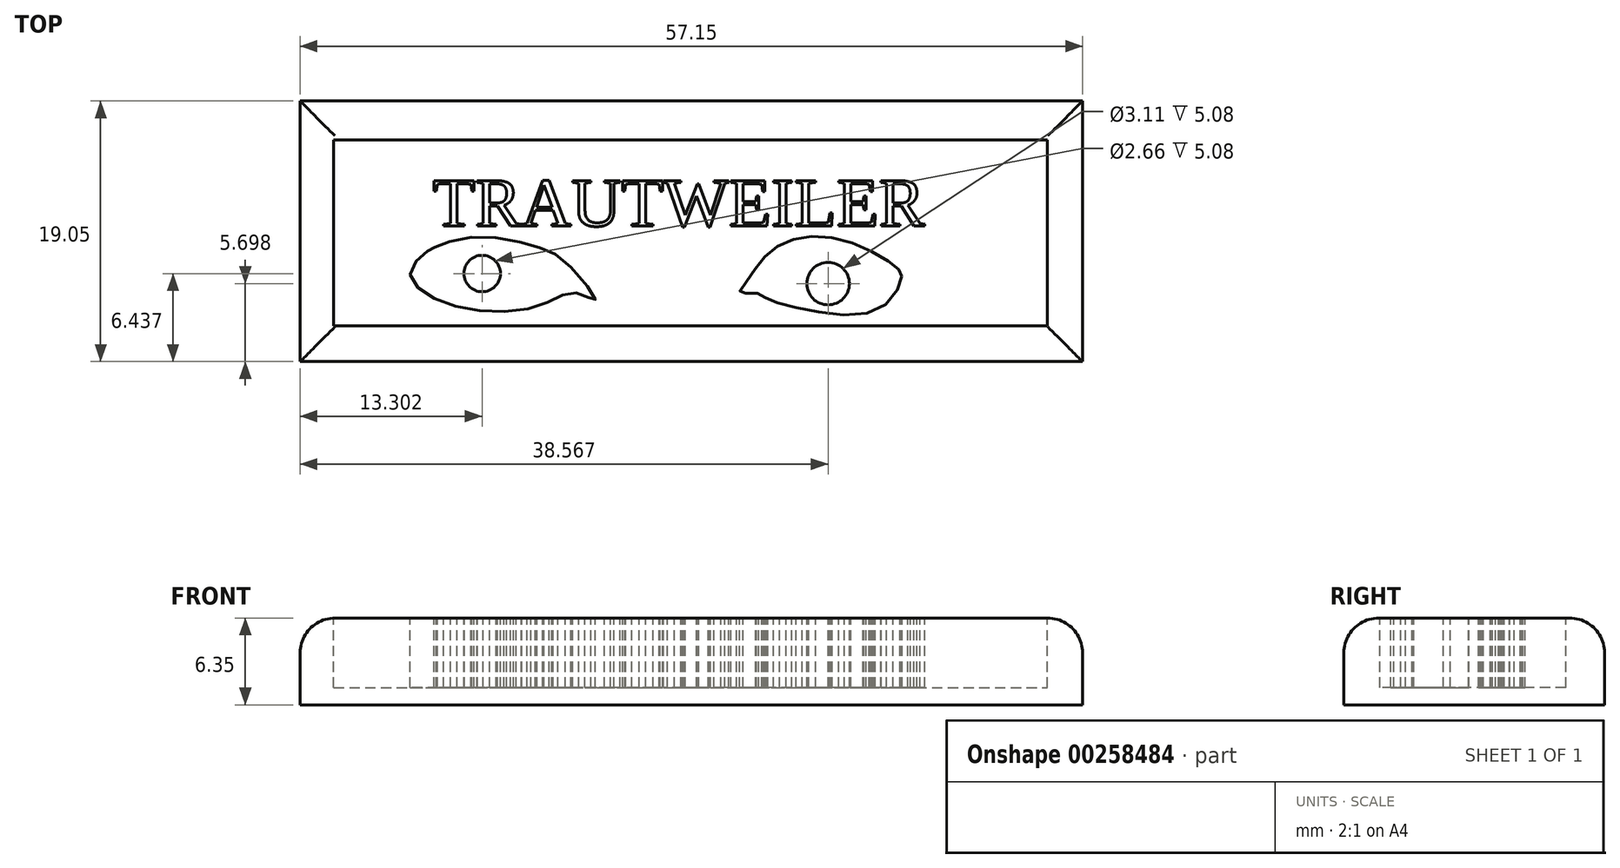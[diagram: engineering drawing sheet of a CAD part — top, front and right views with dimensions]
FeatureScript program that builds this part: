
annotation { "Feature Type Name" : "Feature", "Feature Type Description" : "" }
export const myFeature = defineFeature(function(context is Context, id is Id, definition is map)
    precondition{}
    {
        {
            var Q0;
            Q0=qCreatedBy(makeId("Top.planeOp"),FACE);
            var sketch = newSketch(context, id + "F0", { "sketchPlane" : qUnion([Q0])});
            skLineSegment(sketch, "E0.bottom", {"start": v(-27.46, 2.84) * mm, "end": v(29.7, 2.84) * mm});
            skLineSegment(sketch, "E0.top", {"start": v(-27.46, -16.21) * mm, "end": v(29.7, -16.21) * mm});
            skLineSegment(sketch, "E0.left", {"start": v(-27.46, 2.84) * mm, "end": v(-27.46, -16.21) * mm});
            skLineSegment(sketch, "E0.right", {"start": v(29.7, 2.84) * mm, "end": v(29.7, -16.21) * mm});
            skSolve(sketch);
        }
        {
            var Q0;
            Q0 = qSketchRegion(id + "F0", true);
            extrude(context, id + "F1", {"entities" : qUnion([Q0]), "depth" : 6.35 * mm});
        }
        {
            var Q0;
            Q0=makeQuery(id+"F1.opExtrude","CAP_FACE",FACE,{"disambiguationData":[OSD([sQuery(id+"F0.wireOp",EDGE,"E0.bottom"),sQuery(id+"F0.wireOp",EDGE,"E0.top"),sQuery(id+"F0.wireOp",EDGE,"E0.left"),sQuery(id+"F0.wireOp",EDGE,"E0.right")])],"isStart":false});
            var sketch = newSketch(context, id + "F2", { "sketchPlane" : qUnion([Q0])});
            skSolve(sketch);
        }
        {
            var Q0;
            Q0=makeQuery(id+"F1.opExtrude","CAP_FACE",FACE,{"disambiguationData":[OSD([sQuery(id+"F0.wireOp",EDGE,"E0.bottom"),sQuery(id+"F0.wireOp",EDGE,"E0.top"),sQuery(id+"F0.wireOp",EDGE,"E0.left"),sQuery(id+"F0.wireOp",EDGE,"E0.right")])],"isStart":false});
            fillet(context, id + "F3", {"entities" : qUnion([Q0]), "radius" : 2.54 * mm, "tangentPropagation" : true, "allowEdgeOverflow" : false});
        }
        {
            var Q0;
            Q0=makeQuery(id+"F2.imprint","IMPRINT",FACE,{"disambiguationData":[TD([[makeQuery(id+"F2.imprint","IMPRINT",EDGE,{"derivedFrom":makeQuery(id+"F1.opExtrude","CAP_EDGE",EDGE,{"disambiguationData":[OSD([sQuery(id+"F0.wireOp",EDGE,"E0.bottom")])],"isStart":false})}),-1.0]])]});
            var sketch = newSketch(context, id + "F4", { "sketchPlane" : qUnion([Q0])});
            skText(sketch, "E1", { "text": "TRAUTWEILER", "fontName": "Tinos-Regular.ttf"});
            const initialGuessF4  = {"E1": [-0.0205, -0.00855, 1, 0, 0.00434]};
            skSetInitialGuess(sketch, initialGuessF4);
            skSolve(sketch);
        }
        {
            var Q0;
            Q0 = qSketchRegion(id + "F4", true);
            extrude(context, id + "F5", {"entities" : qUnion([Q0]), "operationType" : NewBodyOperationType.ADD, "oppositeDirection" : true, "depth" : 5.08 * mm});
        }
        {
            var Q0;
            Q0=makeQuery(id+"F2.imprint","IMPRINT",FACE,{"disambiguationData":[TD([[makeQuery(id+"F2.imprint","IMPRINT",EDGE,{"derivedFrom":makeQuery(id+"F1.opExtrude","CAP_EDGE",EDGE,{"disambiguationData":[OSD([sQuery(id+"F0.wireOp",EDGE,"E0.bottom")])],"isStart":false})}),-1.0]])]});
            var sketch = newSketch(context, id + "F6", { "sketchPlane" : qUnion([Q0])});
            skLineSegment(sketch, "E2.bottom", {"start": v(-25, 0) * mm, "end": v(27.13, 0) * mm});
            skLineSegment(sketch, "E2.top", {"start": v(-25, -13.58) * mm, "end": v(27.13, -13.58) * mm});
            skLineSegment(sketch, "E2.left", {"start": v(-25, 0) * mm, "end": v(-25, -13.58) * mm});
            skLineSegment(sketch, "E2.right", {"start": v(27.13, 0) * mm, "end": v(27.13, -13.58) * mm});
            skSolve(sketch);
        }
        {
            var Q0;
            Q0 = qSketchRegion(id + "F6", true);
            extrude(context, id + "F7", {"entities" : qUnion([Q0]), "operationType" : NewBodyOperationType.REMOVE, "oppositeDirection" : true, "depth" : 5.08 * mm});
        }
        {
            var Q0;
            Q0=makeQuery(id+"F2.imprint","IMPRINT",FACE,{"disambiguationData":[TD([[makeQuery(id+"F2.imprint","IMPRINT",EDGE,{"derivedFrom":makeQuery(id+"F1.opExtrude","CAP_EDGE",EDGE,{"disambiguationData":[OSD([sQuery(id+"F0.wireOp",EDGE,"E0.bottom")])],"isStart":false})}),-1.0]])]});
            var sketch = newSketch(context, id + "F8", { "sketchPlane" : qUnion([Q0])});
            skText(sketch, "E3", { "text": "TRAUTWEILER", "fontName": "Tinos-Regular.ttf"});
            const initialGuessF8  = {"E3": [-0.01776, -0.0063, 1, 0, 0.00364]};
            skSetInitialGuess(sketch, initialGuessF8);
            skSolve(sketch);
        }
        {
            var Q0;
            Q0 = qSketchRegion(id + "F8", true);
            extrude(context, id + "F9", {"entities" : qUnion([Q0]), "operationType" : NewBodyOperationType.ADD, "oppositeDirection" : true, "depth" : 6.35 * mm});
        }
        {
            var Q0;
            Q0=makeQuery(id+"F2.imprint","IMPRINT",FACE,{"disambiguationData":[TD([[makeQuery(id+"F2.imprint","IMPRINT",EDGE,{"derivedFrom":makeQuery(id+"F1.opExtrude","CAP_EDGE",EDGE,{"disambiguationData":[OSD([sQuery(id+"F0.wireOp",EDGE,"E0.bottom")])],"isStart":false})}),-1.0]])]});
            var sketch = newSketch(context, id + "F10", { "sketchPlane" : qUnion([Q0])});
            skFitSpline(sketch, "E4", {"points": [v(-18.15, -8.15) * mm, v(-17.63, -7.85) * mm, v(-14.75, -7.11) * mm, v(-10.24, -7.78) * mm, v(-7.88, -9.1) * mm, v(-5.88, -11.7) * mm, v(-6.33, -11.55) * mm, v(-7.73, -11.18) * mm, v(-9.8, -12.06) * mm, v(-14.3, -12.5) * mm, v(-18.37, -11.18) * mm, v(-19.4, -9.55) * mm, v(-18.15, -8.15) * mm]});
            skFitSpline(sketch, "E5", {"points": [v(16.5, -10) * mm, v(16.2, -9.4) * mm, v(13.47, -7.78) * mm, v(9.33, -7.11) * mm, v(6.67, -8.37) * mm, v(5.2, -10.3) * mm, v(4.68, -11.18) * mm, v(5.79, -11.18) * mm, v(6.53, -11.55) * mm, v(9.56, -12.43) * mm, v(14.95, -12.28) * mm, v(16.5, -10) * mm]});
            skSolve(sketch);
        }
        {
            var Q0;
            Q0 = qSketchRegion(id + "F10", true);
            extrude(context, id + "F11", {"entities" : qUnion([Q0]), "operationType" : NewBodyOperationType.ADD, "oppositeDirection" : true, "depth" : 6.35 * mm});
        }
        {
            var Q0;
            Q0=makeQuery(id+"F2.imprint","IMPRINT",FACE,{"disambiguationData":[TD([[makeQuery(id+"F2.imprint","IMPRINT",EDGE,{"derivedFrom":makeQuery(id+"F1.opExtrude","CAP_EDGE",EDGE,{"disambiguationData":[OSD([sQuery(id+"F0.wireOp",EDGE,"E0.bottom")])],"isStart":false})}),-1.0]])]});
            var sketch = newSketch(context, id + "F12", { "sketchPlane" : qUnion([Q0])});
            skCircle(sketch, "E6", {"center": v(-14.16, -9.77) * mm, "radius": 1.33 * mm});
            skCircle(sketch, "E7", {"center": v(11.1, -10.51) * mm, "radius": 1.55 * mm});
            skSolve(sketch);
        }
        {
            var Q0;
            Q0 = qSketchRegion(id + "F12", true);
            extrude(context, id + "F13", {"entities" : qUnion([Q0]), "operationType" : NewBodyOperationType.REMOVE, "oppositeDirection" : true, "depth" : 5.08 * mm});
        }
    });
